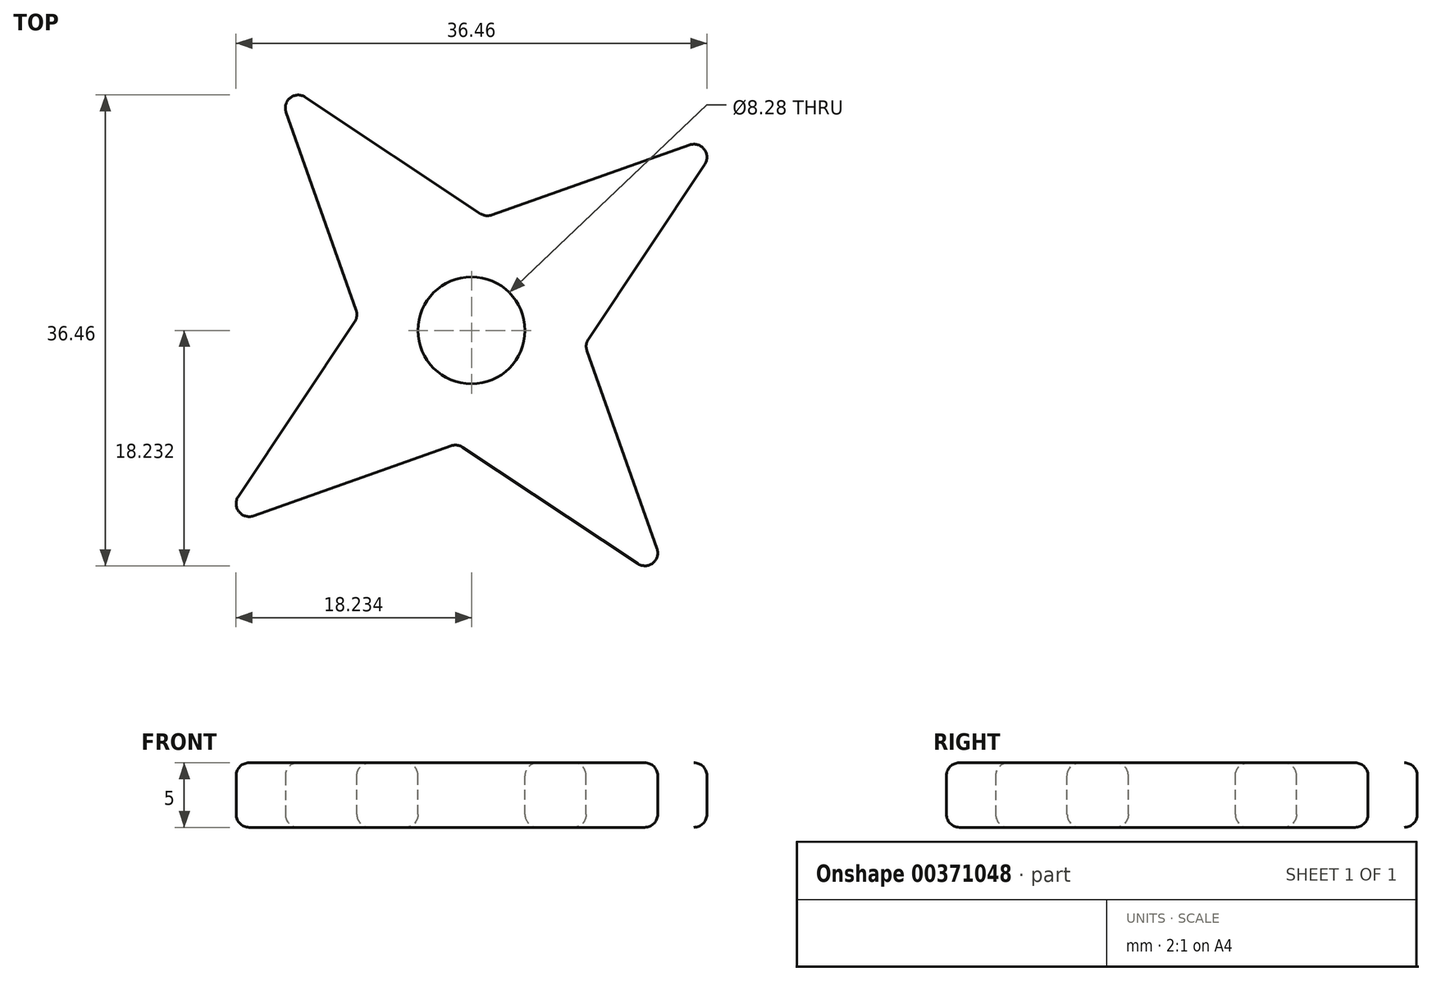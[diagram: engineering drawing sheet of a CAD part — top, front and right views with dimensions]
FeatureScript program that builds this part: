
annotation { "Feature Type Name" : "Feature", "Feature Type Description" : "" }
export const myFeature = defineFeature(function(context is Context, id is Id, definition is map)
    precondition{}
    {
        {
            var Q0;
            Q0=qCreatedBy(makeId("Top.planeOp"),FACE);
            var sketch = newSketch(context, id + "F0", { "sketchPlane" : qUnion([Q0])});
            skLineSegment(sketch, "E0", {"start": v(0, 0) * mm, "end": v(19.72, 15.36) * mm});
            skPoint(sketch, "E1.center", {"position": v(19.72, 15.36) * mm});
            skLineSegment(sketch, "E2.1.0", {"start": v(35.09, -4.36) * mm, "end": v(19.72, 15.36) * mm});
            skLineSegment(sketch, "E2.2.0", {"start": v(39.45, 30.72) * mm, "end": v(19.72, 15.36) * mm});
            skLineSegment(sketch, "E2.3.0", {"start": v(4.36, 35.09) * mm, "end": v(19.72, 15.36) * mm});
            skLineSegment(sketch, "E3", {"start": v(4.36, 35.09) * mm, "end": v(10.95, 16.45) * mm});
            skLineSegment(sketch, "E4", {"start": v(10.95, 16.45) * mm, "end": v(0, 0) * mm});
            skLineSegment(sketch, "E5.1.0", {"start": v(0, 0) * mm, "end": v(18.63, 6.6) * mm});
            skLineSegment(sketch, "E5.1.1", {"start": v(18.63, 6.6) * mm, "end": v(35.09, -4.36) * mm});
            skLineSegment(sketch, "E5.2.0", {"start": v(35.09, -4.36) * mm, "end": v(28.5, 14.27) * mm});
            skLineSegment(sketch, "E5.2.1", {"start": v(28.5, 14.27) * mm, "end": v(39.45, 30.72) * mm});
            skLineSegment(sketch, "E5.3.0", {"start": v(39.45, 30.72) * mm, "end": v(20.81, 24.13) * mm});
            skLineSegment(sketch, "E5.3.1", {"start": v(20.81, 24.13) * mm, "end": v(4.36, 35.09) * mm});
            skSolve(sketch);
        }
        {
            var Q0;
            Q0 = qSketchRegion(id + "F0", true);
            extrude(context, id + "F1", {"entities" : qUnion([Q0]), "depth" : 5 * mm});
        }
        {
            var Q0;
            Q0=makeQuery(id+"F1.opExtrude","CAP_FACE",FACE,{"disambiguationData":[OSD([sQuery(id+"F0.wireOp",EDGE,"E3"),sQuery(id+"F0.wireOp",EDGE,"E4"),sQuery(id+"F0.wireOp",EDGE,"E5.1.0"),sQuery(id+"F0.wireOp",EDGE,"E5.1.1"),sQuery(id+"F0.wireOp",EDGE,"E5.2.0"),sQuery(id+"F0.wireOp",EDGE,"E5.2.1"),sQuery(id+"F0.wireOp",EDGE,"E5.3.0"),sQuery(id+"F0.wireOp",EDGE,"E5.3.1")])],"isStart":false});
            var sketch = newSketch(context, id + "F2", { "sketchPlane" : qUnion([Q0])});
            skLineSegment(sketch, "E6", {"start": v(20.81, 24.13) * mm, "end": v(18.63, 6.6) * mm, "construction": true});
            skLineSegment(sketch, "E7", {"start": v(10.95, 16.45) * mm, "end": v(28.5, 14.27) * mm, "construction": true});
            skCircle(sketch, "E8", {"center": v(19.72, 15.36) * mm, "radius": 4.14 * mm});
            skSolve(sketch);
        }
        {
            var Q0;
            Q0=makeQuery(id+"F2.imprint","IMPRINT",FACE,{"disambiguationData":[TD([[makeQuery(id+"F2.imprint","IMPRINT",EDGE,{"derivedFrom":sQuery(id+"F2.wireOp",EDGE,"E8")}),1.0]])]});
            var Q1;
            Q1=sQuery(id+"F2.wireOp",EDGE,"E8");
            extrude(context, id + "F3", {"entities" : qUnion([Q0]), "operationType" : NewBodyOperationType.REMOVE, "surfaceEntities" : qUnion([Q1]), "oppositeDirection" : true, "depth" : 25 * mm});
        }
        {
            var Q0;
            Q0=makeQuery(id+"F1.opExtrude","CAP_FACE",FACE,{"disambiguationData":[OSD([sQuery(id+"F0.wireOp",EDGE,"E3"),sQuery(id+"F0.wireOp",EDGE,"E4"),sQuery(id+"F0.wireOp",EDGE,"E5.1.0"),sQuery(id+"F0.wireOp",EDGE,"E5.1.1"),sQuery(id+"F0.wireOp",EDGE,"E5.2.0"),sQuery(id+"F0.wireOp",EDGE,"E5.2.1"),sQuery(id+"F0.wireOp",EDGE,"E5.3.0"),sQuery(id+"F0.wireOp",EDGE,"E5.3.1")])],"isStart":false});
            var Q1;
            Q1=makeQuery(id+"F1.opExtrude","CAP_FACE",FACE,{"disambiguationData":[OSD([sQuery(id+"F0.wireOp",EDGE,"E3"),sQuery(id+"F0.wireOp",EDGE,"E4"),sQuery(id+"F0.wireOp",EDGE,"E5.1.0"),sQuery(id+"F0.wireOp",EDGE,"E5.1.1"),sQuery(id+"F0.wireOp",EDGE,"E5.2.0"),sQuery(id+"F0.wireOp",EDGE,"E5.2.1"),sQuery(id+"F0.wireOp",EDGE,"E5.3.0"),sQuery(id+"F0.wireOp",EDGE,"E5.3.1")])],"isStart":true});
            var Q2;
            Q2=makeQuery(id+"F1.opExtrude","SWEPT_FACE",FACE,{"disambiguationData":[OSD([sQuery(id+"F0.wireOp",EDGE,"E5.2.0")])]});
            var Q3;
            Q3=makeQuery(id+"F1.opExtrude","SWEPT_FACE",FACE,{"disambiguationData":[OSD([sQuery(id+"F0.wireOp",EDGE,"E5.2.1")])]});
            var Q4;
            Q4=makeQuery(id+"F1.opExtrude","SWEPT_FACE",FACE,{"disambiguationData":[OSD([sQuery(id+"F0.wireOp",EDGE,"E5.3.1")])]});
            var Q5;
            Q5=makeQuery(id+"F1.opExtrude","SWEPT_FACE",FACE,{"disambiguationData":[OSD([sQuery(id+"F0.wireOp",EDGE,"E4")])]});
            var Q6;
            Q6=makeQuery(id+"F1.opExtrude","SWEPT_EDGE",EDGE,{"disambiguationData":[OSD([sQuery(id+"F0.wireOp",EDGE,"E5.1.0"),sQuery(id+"F0.wireOp",EDGE,"E5.1.1")])]});
            fillet(context, id + "F4", {"entities" : qUnion([Q0, Q1, Q2, Q3, Q4, Q5, Q6]), "radius" : 1 * mm, "tangentPropagation" : true, "allowEdgeOverflow" : false});
        }
    });
